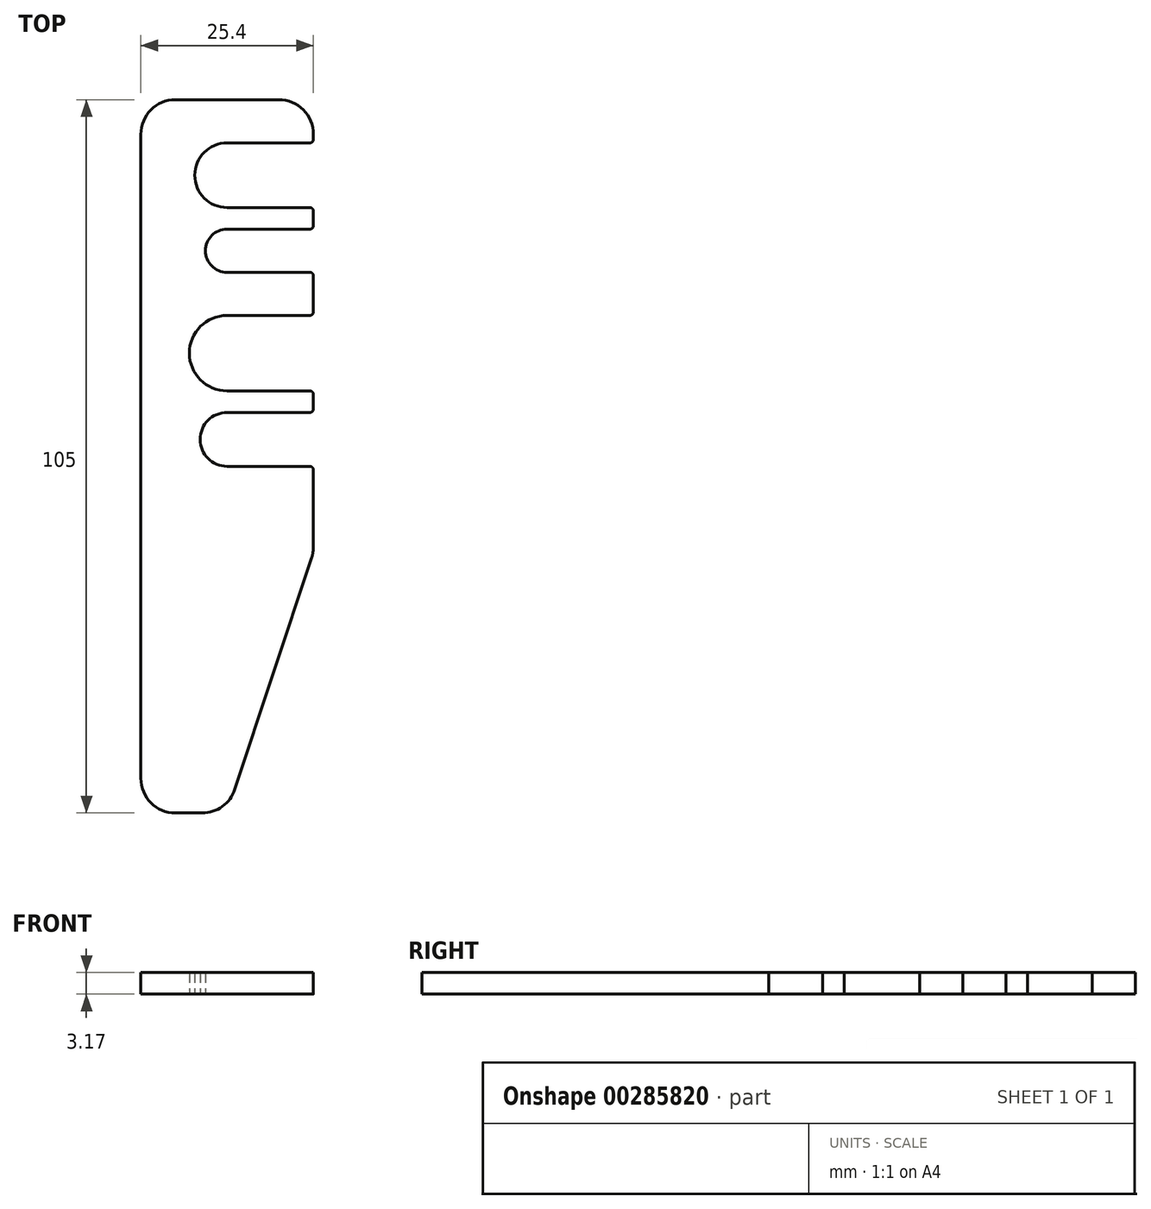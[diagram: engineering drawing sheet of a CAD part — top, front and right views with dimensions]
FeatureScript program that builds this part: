
annotation { "Feature Type Name" : "Feature", "Feature Type Description" : "" }
export const myFeature = defineFeature(function(context is Context, id is Id, definition is map)
    precondition{}
    {
        {
            var Q0;
            Q0=qCreatedBy(makeId("Top.planeOp"),FACE);
            var sketch = newSketch(context, id + "F0", { "sketchPlane" : qUnion([Q0])});
            skLineSegment(sketch, "E0", {"start": v(-30.84, -61.69) * mm, "end": v(-30.84, 43.31) * mm});
            skLineSegment(sketch, "E1", {"start": v(-30.84, 43.31) * mm, "end": v(-5.44, 43.31) * mm});
            skLineSegment(sketch, "E2", {"start": v(-5.44, 43.31) * mm, "end": v(-5.44, 36.96) * mm});
            skLineSegment(sketch, "E3", {"start": v(-5.44, 36.96) * mm, "end": v(-18.14, 36.96) * mm});
            skArc(sketch, "E4", {"start": v(-18.14, 36.96) * mm, "mid": v(-22.9, 32.2) * mm, "end": v(-18.14, 27.44) * mm});
            skLineSegment(sketch, "E5", {"start": v(-18.14, 27.44) * mm, "end": v(-5.44, 27.44) * mm});
            skLineSegment(sketch, "E6", {"start": v(-5.44, 27.44) * mm, "end": v(-5.44, 24.26) * mm});
            skLineSegment(sketch, "E7", {"start": v(-5.44, 24.26) * mm, "end": v(-18.14, 24.26) * mm});
            skArc(sketch, "E8", {"start": v(-18.14, 24.26) * mm, "mid": v(-21.32, 21.09) * mm, "end": v(-18.14, 17.91) * mm});
            skLineSegment(sketch, "E9", {"start": v(-18.14, 17.91) * mm, "end": v(-5.44, 17.91) * mm});
            skLineSegment(sketch, "E10", {"start": v(-5.44, 17.91) * mm, "end": v(-5.44, 11.56) * mm});
            skLineSegment(sketch, "E11", {"start": v(-5.44, 11.56) * mm, "end": v(-18.14, 11.56) * mm});
            skArc(sketch, "E12", {"start": v(-18.14, 11.56) * mm, "mid": v(-23.7, 6) * mm, "end": v(-18.14, 0.45) * mm});
            skLineSegment(sketch, "E13", {"start": v(-18.14, 0.45) * mm, "end": v(-5.44, 0.45) * mm});
            skLineSegment(sketch, "E14", {"start": v(-5.44, 0.45) * mm, "end": v(-5.44, -2.72) * mm});
            skLineSegment(sketch, "E15", {"start": v(-5.44, -2.72) * mm, "end": v(-18.14, -2.72) * mm});
            skArc(sketch, "E16", {"start": v(-18.14, -2.72) * mm, "mid": v(-22.1, -6.7) * mm, "end": v(-18.14, -10.66) * mm});
            skLineSegment(sketch, "E17", {"start": v(-18.14, -10.66) * mm, "end": v(-5.44, -10.66) * mm});
            skLineSegment(sketch, "E18", {"start": v(-5.44, -10.66) * mm, "end": v(-5.44, -23.36) * mm});
            skLineSegment(sketch, "E19", {"start": v(-30.84, -61.69) * mm, "end": v(-18.14, -61.69) * mm});
            skLineSegment(sketch, "E20", {"start": v(-18.14, -61.69) * mm, "end": v(-5.44, -23.36) * mm});
            skSolve(sketch);
        }
        {
            var Q0;
            Q0=qSketchRegion(id+"F0",true);
            extrude(context, id + "F1", {"entities" : qUnion([Q0]), "depth" : 3.17 * mm});
        }
        {
            var Q0;
            Q0=makeQuery(id+"F1.opExtrude","SWEPT_EDGE",EDGE,{"disambiguationData":[OSD([sQuery(id+"F0.wireOp",EDGE,"E19"),sQuery(id+"F0.wireOp",EDGE,"E20")])]});
            var Q1;
            Q1=makeQuery(id+"F1.opExtrude","SWEPT_EDGE",EDGE,{"disambiguationData":[OSD([sQuery(id+"F0.wireOp",EDGE,"E18"),sQuery(id+"F0.wireOp",EDGE,"E20")])]});
            var Q2;
            Q2=makeQuery(id+"F1.opExtrude","SWEPT_EDGE",EDGE,{"disambiguationData":[OSD([sQuery(id+"F0.wireOp",EDGE,"E0"),sQuery(id+"F0.wireOp",EDGE,"E19")])]});
            var Q3;
            Q3=makeQuery(id+"F1.opExtrude","SWEPT_EDGE",EDGE,{"disambiguationData":[OSD([sQuery(id+"F0.wireOp",EDGE,"E1"),sQuery(id+"F0.wireOp",EDGE,"E2")])]});
            var Q4;
            Q4=makeQuery(id+"F1.opExtrude","SWEPT_EDGE",EDGE,{"disambiguationData":[OSD([sQuery(id+"F0.wireOp",EDGE,"E0"),sQuery(id+"F0.wireOp",EDGE,"E1")])]});
            fillet(context, id + "F2", {"entities" : qUnion([Q0, Q1, Q2, Q3, Q4]), "radius" : 5.08 * mm, "tangentPropagation" : true, "allowEdgeOverflow" : false});
        }
        {
            var Q0;
            Q0=makeQuery(id+"F1.opExtrude","SWEPT_EDGE",EDGE,{"disambiguationData":[OSD([sQuery(id+"F0.wireOp",EDGE,"E17"),sQuery(id+"F0.wireOp",EDGE,"E18")])]});
            var Q1;
            Q1=makeQuery(id+"F1.opExtrude","SWEPT_EDGE",EDGE,{"disambiguationData":[OSD([sQuery(id+"F0.wireOp",EDGE,"E14"),sQuery(id+"F0.wireOp",EDGE,"E15")])]});
            var Q2;
            Q2=makeQuery(id+"F1.opExtrude","SWEPT_EDGE",EDGE,{"disambiguationData":[OSD([sQuery(id+"F0.wireOp",EDGE,"E13"),sQuery(id+"F0.wireOp",EDGE,"E14")])]});
            var Q3;
            Q3=makeQuery(id+"F1.opExtrude","SWEPT_EDGE",EDGE,{"disambiguationData":[OSD([sQuery(id+"F0.wireOp",EDGE,"E10"),sQuery(id+"F0.wireOp",EDGE,"E11")])]});
            var Q4;
            Q4=makeQuery(id+"F1.opExtrude","SWEPT_EDGE",EDGE,{"disambiguationData":[OSD([sQuery(id+"F0.wireOp",EDGE,"E9"),sQuery(id+"F0.wireOp",EDGE,"E10")])]});
            var Q5;
            Q5=makeQuery(id+"F1.opExtrude","SWEPT_EDGE",EDGE,{"disambiguationData":[OSD([sQuery(id+"F0.wireOp",EDGE,"E6"),sQuery(id+"F0.wireOp",EDGE,"E7")])]});
            var Q6;
            Q6=makeQuery(id+"F1.opExtrude","SWEPT_EDGE",EDGE,{"disambiguationData":[OSD([sQuery(id+"F0.wireOp",EDGE,"E5"),sQuery(id+"F0.wireOp",EDGE,"E6")])]});
            var Q7;
            Q7=makeQuery(id+"F1.opExtrude","SWEPT_EDGE",EDGE,{"disambiguationData":[OSD([sQuery(id+"F0.wireOp",EDGE,"E2"),sQuery(id+"F0.wireOp",EDGE,"E3")])]});
            fillet(context, id + "F3", {"entities" : qUnion([Q0, Q1, Q2, Q3, Q4, Q5, Q6, Q7]), "radius" : 0.5 * mm, "tangentPropagation" : true, "allowEdgeOverflow" : false});
        }
    });
